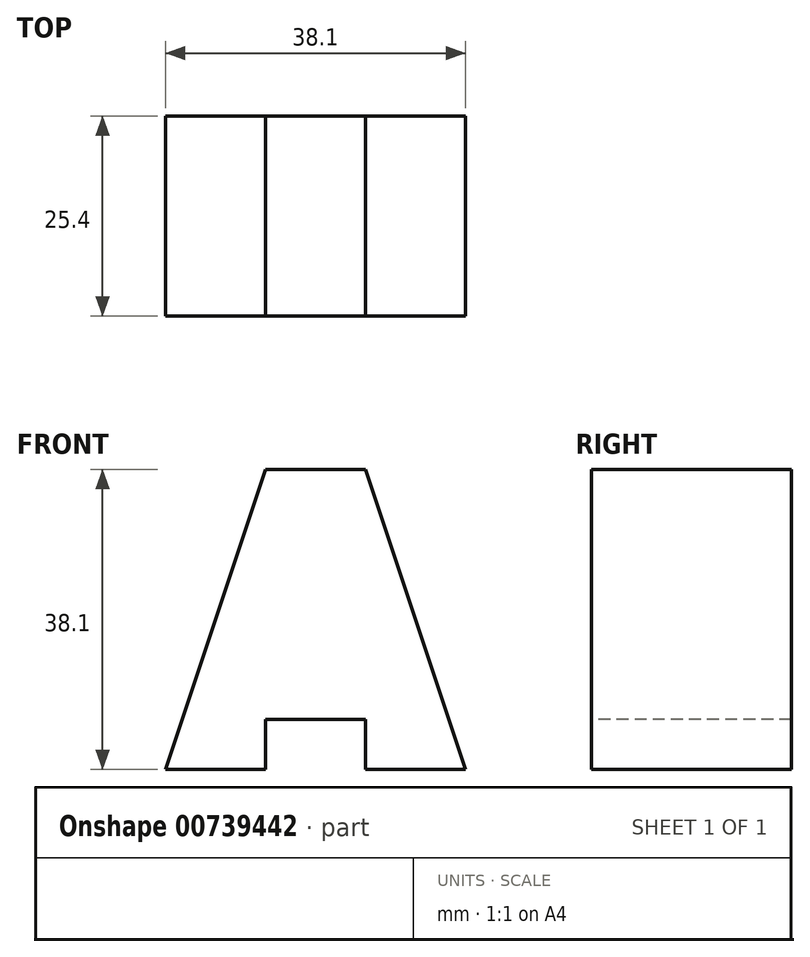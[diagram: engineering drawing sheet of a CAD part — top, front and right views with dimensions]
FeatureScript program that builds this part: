
annotation { "Feature Type Name" : "Feature", "Feature Type Description" : "" }
export const myFeature = defineFeature(function(context is Context, id is Id, definition is map)
    precondition{}
    {
        {
            var Q0;
            Q0=qCreatedBy(makeId("Front.planeOp"),FACE);
            var sketch = newSketch(context, id + "F0", { "sketchPlane" : qUnion([Q0])});
            skLineSegment(sketch, "E0", {"start": v(0, 0) * mm, "end": v(38.1, 0) * mm});
            skLineSegment(sketch, "E1", {"start": v(38.1, 0) * mm, "end": v(38.1, 38.1) * mm});
            skLineSegment(sketch, "E2", {"start": v(38.1, 38.1) * mm, "end": v(0, 38.1) * mm});
            skLineSegment(sketch, "E3", {"start": v(0, 38.1) * mm, "end": v(0, 0) * mm});
            skSolve(sketch);
        }
        {
            var Q0;
            Q0=makeQuery(id+"F0.imprint","IMPRINT",FACE,{"disambiguationData":[TD([[makeQuery(id+"F0.imprint","IMPRINT",EDGE,{"derivedFrom":sQuery(id+"F0.wireOp",EDGE,"E0")}),1.0]])]});
            extrude(context, id + "F1", {"entities" : qUnion([Q0]), "depth" : 25.4 * mm, "offsetDistance" : 25.4 * mm});
        }
        {
            var Q0;
            Q0=makeQuery(id+"F1.opExtrude","CAP_FACE",FACE,{"disambiguationData":[OSD([sQuery(id+"F0.wireOp",EDGE,"E0"),sQuery(id+"F0.wireOp",EDGE,"E1"),sQuery(id+"F0.wireOp",EDGE,"E2"),sQuery(id+"F0.wireOp",EDGE,"E3")])],"isStart":false});
            var sketch = newSketch(context, id + "F2", { "sketchPlane" : qUnion([Q0])});
            skLineSegment(sketch, "E4", {"start": v(25.4, 38.1) * mm, "end": v(38.1, 0) * mm});
            skLineSegment(sketch, "E5", {"start": v(38.1, 0) * mm, "end": v(38.1, 38.1) * mm});
            skLineSegment(sketch, "E6", {"start": v(38.1, 38.1) * mm, "end": v(25.4, 38.1) * mm});
            skLineSegment(sketch, "E7", {"start": v(0, 38.1) * mm, "end": v(0, 0) * mm});
            skLineSegment(sketch, "E8", {"start": v(0, 0) * mm, "end": v(12.7, 38.1) * mm});
            skLineSegment(sketch, "E9", {"start": v(12.7, 38.1) * mm, "end": v(0, 38.1) * mm});
            skSolve(sketch);
        }
        {
            var Q0;
            Q0=makeQuery(id+"F2.imprint","IMPRINT",FACE,{"disambiguationData":[TD([[makeQuery(id+"F2.imprint","IMPRINT",EDGE,{"derivedFrom":sQuery(id+"F2.wireOp",EDGE,"E7")}),1.0]])]});
            var Q1;
            Q1=makeQuery(id+"F2.imprint","IMPRINT",FACE,{"disambiguationData":[TD([[makeQuery(id+"F2.imprint","IMPRINT",EDGE,{"derivedFrom":sQuery(id+"F2.wireOp",EDGE,"E4")}),1.0]])]});
            extrude(context, id + "F3", {"entities" : qUnion([Q0, Q1]), "operationType" : NewBodyOperationType.REMOVE, "oppositeDirection" : true, "depth" : 25.4 * mm, "offsetDistance" : 25.4 * mm});
        }
        {
            var Q0;
            Q0=makeQuery(id+"F1.opExtrude","CAP_FACE",FACE,{"disambiguationData":[OSD([sQuery(id+"F0.wireOp",EDGE,"E0"),sQuery(id+"F0.wireOp",EDGE,"E1"),sQuery(id+"F0.wireOp",EDGE,"E2"),sQuery(id+"F0.wireOp",EDGE,"E3")])],"isStart":false});
            var sketch = newSketch(context, id + "F4", { "sketchPlane" : qUnion([Q0])});
            skLineSegment(sketch, "E10", {"start": v(12.7, 0) * mm, "end": v(12.7, 6.35) * mm});
            skLineSegment(sketch, "E11", {"start": v(12.7, 6.35) * mm, "end": v(25.4, 6.35) * mm});
            skLineSegment(sketch, "E12", {"start": v(25.4, 6.35) * mm, "end": v(25.4, 0) * mm});
            skLineSegment(sketch, "E13", {"start": v(25.4, 0) * mm, "end": v(12.7, 0) * mm});
            skSolve(sketch);
        }
        {
            var Q0;
            Q0=makeQuery(id+"F4.imprint","IMPRINT",FACE,{"disambiguationData":[TD([[makeQuery(id+"F4.imprint","IMPRINT",EDGE,{"derivedFrom":sQuery(id+"F4.wireOp",EDGE,"E10")}),-1.0]])]});
            extrude(context, id + "F5", {"entities" : qUnion([Q0]), "operationType" : NewBodyOperationType.REMOVE, "oppositeDirection" : true, "depth" : 25.4 * mm, "offsetDistance" : 25.4 * mm});
        }
    });
